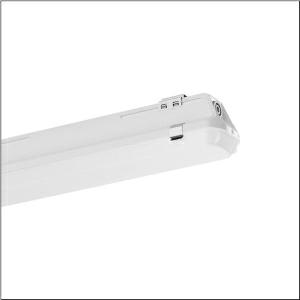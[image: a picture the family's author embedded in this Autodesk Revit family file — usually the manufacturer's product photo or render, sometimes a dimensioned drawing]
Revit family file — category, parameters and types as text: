
# Revit family: monsun_r__11_51fp207p460h_8ebd
name_source: partatom
category: Lighting Fixtures
units: mm (PartAtom-declared; Revit-internal decimal feet)

## family parameters
Cut with Voids When Loaded = No
Host = Face
Light Source = No
Part Type = Normal
Room Calculation Point = No
Round Connector Dimension = Use Diameter
Shared = No

## types (1)
- Monsun® 11 (1 x LED, 6030 lm, 37.7 W, 4000K)
    Apparent Load = 38 VA
    CIE Flux Codes = 45 75 93 94 100
    Color Rendering = 80
    Color Temperature = 4000K
    Default Elevation = 1800 mm
    Description = Monsun® 11, damp-proof luminaire, chain hanger, primary optical cover: enclosure, of PC, light emission: direct distribution, primary light characteristic: symmetric, installation type: suspended mounting, surface-mounted, horizontal mounting, vertical mounting, LED, rated luminous flux: 6.030lm, luminous efficacy: 160lm/W, light colour: 840, colour temperature: 4000K, control gear: ECG, with terminal, 3-pole, max. 2.5mm², mains connection: 220..240V, AC, 50/60Hz, rated input power: 38W, luminaire housing, of glass-fibre reinforced polyester, uncoated, bright grey, incl. chain hanger, length: 1.590mm, width: 90mm, height: 88mm, clip for enclosure, of stainless steel (V2A), ceiling mounting element, of stainless steel (V2A), chain hanger, of stainless steel (V2A), protection rating (complete): IP66, insulation class (complete): insulation class I (protective earthing), certification: CE, ENEC, VDE, UKCA, protection symbol: D, impact resistance: IK08, permissible operating ambient temperature: -35..+40°C, standard: EN 50419, EN 60598-2-1, no direct snow, no direct sun, no direct rain, for indoor or canopied outdoor use, corresponds to IFS (International Featured Standards) requirements for safety and quality in the food industry, contact your sales advisor before using the luminaires in applications with unclear chemical exposure, large temperature fluctuations or condensation-forming humidity, LABS conformity tested according to VDMA 24364:2018-05, packaging unit: 1 piece
    Height = 89 mm
    Lamp = 1 x LED
    Lamp Light Flux = 6030 lm
    Lamp Power = 37.7 W
    Lamp count = 1
    Length = 1590 mm
    Luminous efficacy = 160 lm/W
    Manufacturer = Siteco
    ModVariant = No
    Model = 51FP207P460H
    Mounting Place = Ceiling
    Mounting Type = Surface mounted
    Number of Poles = 1
    OnlyDefault = Yes
    Power Factor = 1
    Product Name = Monsun® 11
    Product group = damp-proof luminaire
    ProductGroupID = 300
    Protection Class = Protection class I
    Protection Degree = IP 66
    RLX_Detail_Level = 1
    RLX_Emergency_Light_Flux = 0 lm
    RLX_Emergency_Type = 0
    RLX_Emergency_Type_DB = No
    RlxData = <blob elided: 88497 chars, md5=874b5fb5>
    Socket = socket
    Standby Power = 0 W
    System Light Flux = 6030 lm
    System Power = 38 W
    Type Comments = Product without accessories
    Type Image = l_1319650.jpg
    URL = http://relux.com
    VarID = ---
    Voltage = 0 V
    Weight = 0.00 kg
    Width = 90 mm

## geometry (parser evidence)
native form markers: Blend x4, Sweep x14
no freeform markers — native parametric forms only
